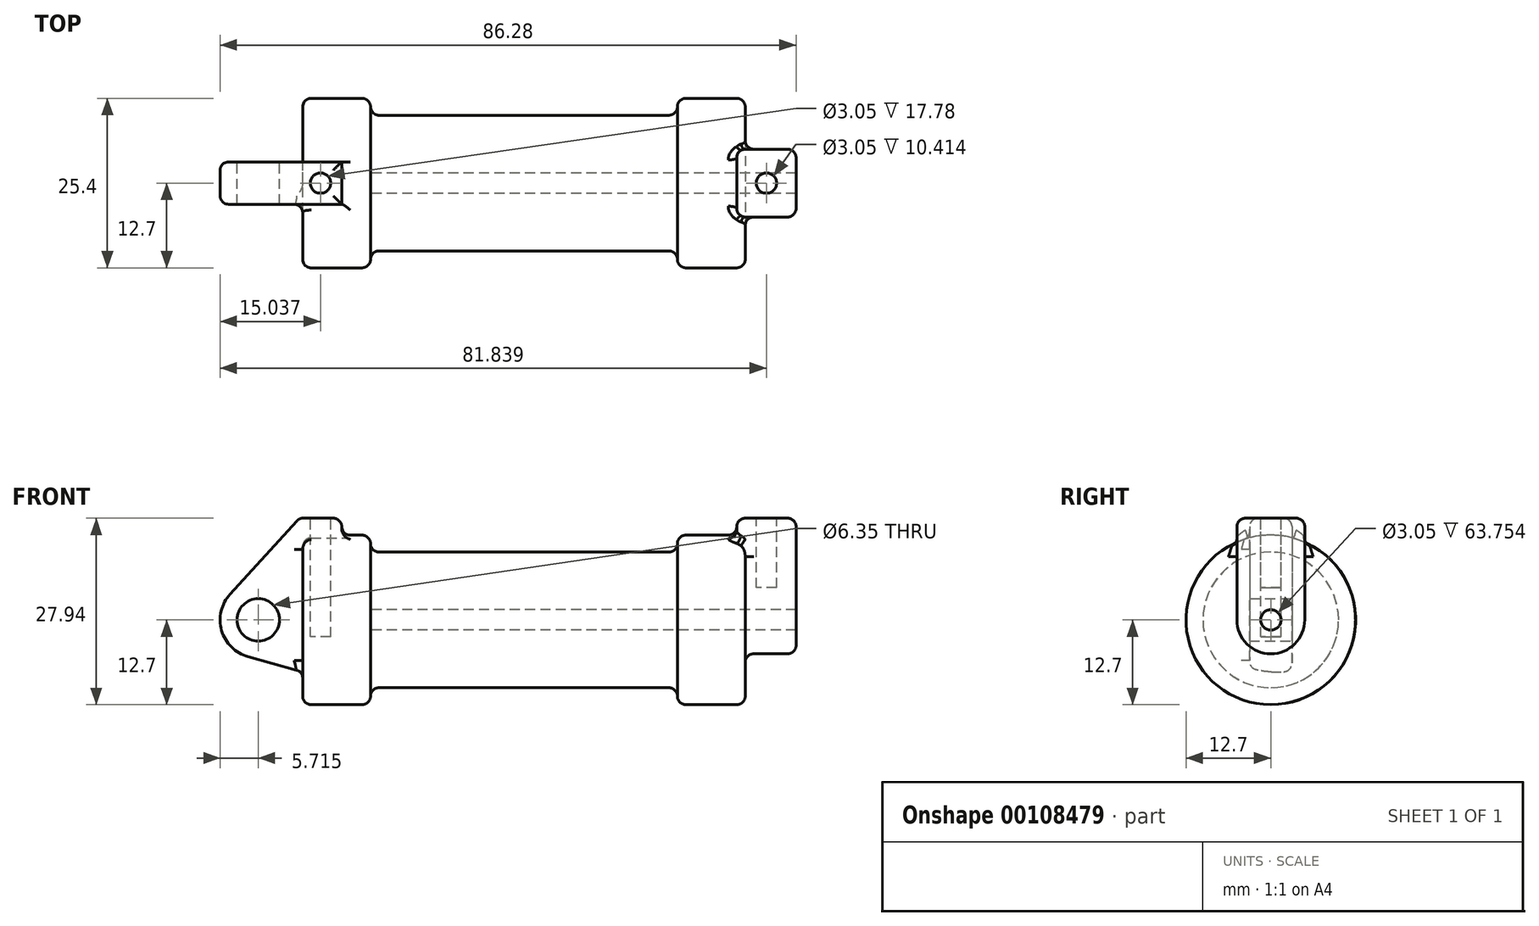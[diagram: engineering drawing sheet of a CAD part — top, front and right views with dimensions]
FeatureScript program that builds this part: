
annotation { "Feature Type Name" : "Feature", "Feature Type Description" : "" }
export const myFeature = defineFeature(function(context is Context, id is Id, definition is map)
    precondition{}
    {
        {
            var Q0;
            Q0=qCreatedBy(makeId("Front.planeOp"),FACE);
            var sketch = newSketch(context, id + "F0", { "sketchPlane" : qUnion([Q0])});
            skLineSegment(sketch, "E0", {"start": v(0, 0) * mm, "end": v(0, 12.7) * mm});
            skLineSegment(sketch, "E1", {"start": v(0, 12.7) * mm, "end": v(10.16, 12.7) * mm});
            skLineSegment(sketch, "E2", {"start": v(10.16, 12.7) * mm, "end": v(10.16, 10.16) * mm});
            skLineSegment(sketch, "E3", {"start": v(10.16, 10.16) * mm, "end": v(56.13, 10.16) * mm});
            skLineSegment(sketch, "E4", {"start": v(56.13, 10.16) * mm, "end": v(56.13, 12.7) * mm});
            skLineSegment(sketch, "E5", {"start": v(56.13, 12.7) * mm, "end": v(66.3, 12.7) * mm});
            skLineSegment(sketch, "E6", {"start": v(66.3, 12.7) * mm, "end": v(66.3, 0) * mm});
            skLineSegment(sketch, "E7", {"start": v(66.3, 0) * mm, "end": v(0, 0) * mm});
            skLineSegment(sketch, "E8", {"start": v(5.84, 15.24) * mm, "end": v(-0.5, 15.24) * mm});
            skLineSegment(sketch, "E9", {"start": v(-0.5, 15.24) * mm, "end": v(-10.88, 3.85) * mm});
            skLineSegment(sketch, "E10", {"start": v(0, 0) * mm, "end": v(-6.65, 0) * mm});
            skCircle(sketch, "E11", {"center": v(-6.65, 0) * mm, "radius": 5.72 * mm});
            skCircle(sketch, "E12", {"center": v(-6.65, 0) * mm, "radius": 3.18 * mm});
            skLineSegment(sketch, "E13", {"start": v(5.84, 15.24) * mm, "end": v(5.84, -9.4) * mm});
            skLineSegment(sketch, "E14", {"start": v(5.84, -9.4) * mm, "end": v(-8.18, -5.5) * mm});
            skSolve(sketch);
        }
        {
            var Q0;
            {var subQ0=sQuery(id+"F0.wireOp",EDGE,"E2");Q0=makeQuery(id+"F0.imprint","IMPRINT",FACE,{"disambiguationData":[TD([[makeQuery(id+"F0.imprint","IMPRINT",EDGE,{"derivedFrom":subQ0}),-1.0]])]});}
            var Q1;
            {var subQ0=sQuery(id+"F0.wireOp",EDGE,"E0");Q1=makeQuery(id+"F0.imprint","IMPRINT",FACE,{"disambiguationData":[TD([[makeQuery(id+"F0.imprint","IMPRINT",EDGE,{"derivedFrom":subQ0}),-1.0]])]});}
            var Q2;
            Q2=sQuery(id+"F0.wireOp",EDGE,"E7");
            revolve(context, id + "F1", {"entities" : qUnion([Q0, Q1]), "axis" : qUnion([Q2]), "revolveType" : RevolveType.FULL});
        }
        {
            var Q0;
            {var subQ3=sQuery(id+"F0.wireOp",EDGE,"E0");Q0=makeQuery(id+"F0.imprint","IMPRINT",FACE,{"disambiguationData":[TD([[makeQuery(id+"F0.imprint","IMPRINT",EDGE,{"derivedFrom":subQ3}),1.0]])]});}
            var Q1;
            {var subQ0=sQuery(id+"F0.wireOp",EDGE,"E14");Q1=makeQuery(id+"F0.imprint","IMPRINT",FACE,{"disambiguationData":[TD([[makeQuery(id+"F0.imprint","IMPRINT",EDGE,{"derivedFrom":subQ0}),-1.0]])]});}
            var Q2;
            {var subQ0=sQuery(id+"F0.wireOp",EDGE,"E0");Q2=makeQuery(id+"F0.imprint","IMPRINT",FACE,{"disambiguationData":[TD([[makeQuery(id+"F0.imprint","IMPRINT",EDGE,{"derivedFrom":subQ0}),-1.0]])]});}
            var Q3;
            {var subQ4=sQuery(id+"F0.wireOp",EDGE,"E12");Q3=makeQuery(id+"F0.imprint","IMPRINT",FACE,{"disambiguationData":[TD([[makeQuery(id+"F0.imprint","IMPRINT",EDGE,{"derivedFrom":subQ4}),-1.0]])]});}
            extrude(context, id + "F2", {"entities" : qUnion([Q0, Q1, Q2, Q3]), "operationType" : NewBodyOperationType.ADD, "endBound" : BoundingType.SYMMETRIC, "depth" : 6.35 * mm});
        }
        {
            var Q0;
            Q0=makeQuery(id+"F1.opRevolve","SWEPT_FACE",FACE,{"disambiguationData":[OSD([sQuery(id+"F0.wireOp",EDGE,"E6")])]});
            var sketch = newSketch(context, id + "F3", { "sketchPlane" : qUnion([Q0])});
            skCircle(sketch, "E15", {"center": v(0, 0) * mm, "radius": 5.08 * mm});
            skLineSegment(sketch, "E16", {"start": v(-5.08, 0) * mm, "end": v(-5.08, 15.24) * mm});
            skLineSegment(sketch, "E17", {"start": v(-5.08, 15.24) * mm, "end": v(5.08, 15.24) * mm});
            skLineSegment(sketch, "E18", {"start": v(5.08, 15.24) * mm, "end": v(5.08, 0) * mm});
            skCircle(sketch, "E19", {"center": v(0, 0) * mm, "radius": 1.52 * mm});
            skSolve(sketch);
        }
        {
            var Q0;
            {var subQ0=sQuery(id+"F3.wireOp",EDGE,"E17");Q0=makeQuery(id+"F3.imprint","IMPRINT",FACE,{"disambiguationData":[TD([[makeQuery(id+"F3.imprint","IMPRINT",EDGE,{"derivedFrom":subQ0}),-1.0]])]});}
            extrude(context, id + "F4", {"entities" : qUnion([Q0]), "operationType" : NewBodyOperationType.ADD, "oppositeDirection" : true, "depth" : 1.27 * mm});
        }
        {
            var Q0;
            Q0=makeQuery(id+"F4.opExtrude","CAP_FACE",FACE,{"disambiguationData":[OSD([sQuery(id+"F0.wireOp",EDGE,"E5"),sQuery(id+"F0.wireOp",EDGE,"E6"),sQuery(id+"F3.wireOp",EDGE,"E16"),sQuery(id+"F3.wireOp",EDGE,"E17"),sQuery(id+"F3.wireOp",EDGE,"E18")])],"isStart":false});
            var Q1;
            Q1 = qSketchRegion(id + "F3", true);
            extrude(context, id + "F5", {"entities" : qUnion([Q0, Q1]), "operationType" : NewBodyOperationType.ADD, "oppositeDirection" : true, "depth" : 7.62 * mm});
        }
        {
            var Q0;
            {var subQ0=sQuery(id+"F0.wireOp",EDGE,"E6");Q0=makeQuery(id+"F5.boolean.opBoolean","SPLIT",FACE,{"disambiguationData":[TD([makeQuery(id+"F5.opExtrude","SWEPT_FACE",FACE,{"disambiguationData":[OSD([sQuery(id+"F3.wireOp",EDGE,"E19")])]})])],"derivedFrom":makeQuery(id+"F4.boolean.opBoolean","MERGE",FACE,{"derivedFrom":[makeQuery(id+"F1.opRevolve","SWEPT_FACE",FACE,{"disambiguationData":[OSD([subQ0])]}),makeQuery(id+"F4.opExtrude","CAP_FACE",FACE,{"disambiguationData":[OSD([sQuery(id+"F0.wireOp",EDGE,"E5"),subQ0,sQuery(id+"F3.wireOp",EDGE,"E16"),sQuery(id+"F3.wireOp",EDGE,"E17"),sQuery(id+"F3.wireOp",EDGE,"E18")])],"isStart":true})]})});}
            var Q1;
            Q1=makeQuery(id+"F1.opRevolve","SWEPT_FACE",FACE,{"disambiguationData":[OSD([sQuery(id+"F0.wireOp",EDGE,"E2")])]});
            extrude(context, id + "F6", {"entities" : qUnion([Q0]), "operationType" : NewBodyOperationType.REMOVE, "endBound" : BoundingType.UP_TO_SURFACE, "oppositeDirection" : true, "endBoundEntityFace" : qUnion([Q1]), "depth" : 25.4 * mm});
        }
        {
            var Q0;
            Q0=makeQuery(id+"F2.opExtrude","SWEPT_FACE",FACE,{"disambiguationData":[OSD([sQuery(id+"F0.wireOp",EDGE,"E8")])]});
            var sketch = newSketch(context, id + "F7", { "sketchPlane" : qUnion([Q0])});
            skCircle(sketch, "E20", {"center": v(2.67, 0) * mm, "radius": 1.52 * mm});
            skPoint(sketch, "E20.centerSnap0", {"position": v(2.67, 3.18) * mm});
            skPoint(sketch, "E21.centerSnap0", {"position": v(5.84, 0) * mm});
            skSolve(sketch);
        }
        {
            var Q0;
            Q0 = qSketchRegion(id + "F7", true);
            extrude(context, id + "F8", {"entities" : qUnion([Q0]), "operationType" : NewBodyOperationType.REMOVE, "oppositeDirection" : true, "depth" : 17.78 * mm});
        }
        {
            var Q0;
            {var subQ0=sQuery(id+"F3.wireOp",EDGE,"E17");Q0=makeQuery(id+"FdJpuOExB23OV29_2.boolean.opBoolean","MERGE",FACE,{"derivedFrom":[makeQuery(id+"F4.opExtrude","SWEPT_FACE",FACE,{"disambiguationData":[OSD([subQ0])]}),makeQuery(id+"FdJpuOExB23OV29_2.opExtrude","SWEPT_FACE",FACE,{"disambiguationData":[OSD([subQ0]),TDD([makeQuery(id+"F3.imprint","IMPRINT",EDGE,{"derivedFrom":subQ0})])]}),makeQuery(id+"FdJpuOExB23OV29_2.opExtrude","SWEPT_FACE",FACE,{"disambiguationData":[OSD([subQ0]),TDD([makeQuery(id+"F4.opExtrude","CAP_EDGE",EDGE,{"disambiguationData":[OSD([subQ0])],"isStart":false})])]})]});}
            var sketch = newSketch(context, id + "F9", { "sketchPlane" : qUnion([Q0])});
            skCircle(sketch, "E22", {"center": v(69.47, 0) * mm, "radius": 1.52 * mm});
            skPoint(sketch, "E22.centerSnap0", {"position": v(69.47, 5.08) * mm});
            skSolve(sketch);
        }
        {
            var Q0;
            Q0 = qSketchRegion(id + "F9", true);
            extrude(context, id + "F10", {"entities" : qUnion([Q0]), "operationType" : NewBodyOperationType.REMOVE, "oppositeDirection" : true, "depth" : 10.4 * mm});
        }
        {
            var Q0;
            Q0=makeQuery(id+"F1.opRevolve","SWEPT_FACE",FACE,{"disambiguationData":[OSD([sQuery(id+"F0.wireOp",EDGE,"E3")])]});
            var Q1;
            Q1=makeQuery(id+"F1.opRevolve","SWEPT_EDGE",EDGE,{"disambiguationData":[OSD([sQuery(id+"F0.wireOp",EDGE,"E1"),sQuery(id+"F0.wireOp",EDGE,"E2")])]});
            var Q2;
            Q2=makeQuery(id+"F1.opRevolve","SWEPT_EDGE",EDGE,{"disambiguationData":[OSD([sQuery(id+"F0.wireOp",EDGE,"E4"),sQuery(id+"F0.wireOp",EDGE,"E5")])]});
            var Q3;
            Q3=makeQuery(id+"F1.opRevolve","SWEPT_EDGE",EDGE,{"disambiguationData":[OSD([sQuery(id+"F0.wireOp",EDGE,"E0"),sQuery(id+"F0.wireOp",EDGE,"E1")])]});
            var Q4;
            Q4=makeQuery(id+"FdJpuOExB23OV29_2.boolean.opBoolean","SPLIT",EDGE,{"disambiguationData":[OD(1.0)],"derivedFrom":makeQuery(id+"F1.opRevolve","SWEPT_EDGE",EDGE,{"disambiguationData":[OSD([sQuery(id+"F0.wireOp",EDGE,"E5"),sQuery(id+"F0.wireOp",EDGE,"E6")])]})});
            fillet(context, id + "F11", {"entities" : qUnion([Q0, Q1, Q2, Q3, Q4]), "radius" : 1.27 * mm, "tangentPropagation" : true, "allowEdgeOverflow" : false});
        }
        {
            var Q0;
            Q0=makeQuery(id+"F2.opExtrude","SWEPT_FACE",FACE,{"disambiguationData":[OSD([sQuery(id+"F0.wireOp",EDGE,"E9")])]});
            var Q1;
            Q1=makeQuery(id+"F2.opExtrude","CAP_EDGE",EDGE,{"disambiguationData":[OSD([sQuery(id+"F0.wireOp",EDGE,"E8")])],"isStart":false});
            var Q2;
            Q2=makeQuery(id+"F2.opExtrude","SWEPT_EDGE",EDGE,{"disambiguationData":[OSD([sQuery(id+"F0.wireOp",EDGE,"E8"),sQuery(id+"F0.wireOp",EDGE,"E13")])]});
            var Q3;
            Q3=makeQuery(id+"F2.opExtrude","CAP_EDGE",EDGE,{"disambiguationData":[OSD([sQuery(id+"F0.wireOp",EDGE,"E8")])],"isStart":true});
            var Q4;
            Q4=makeQuery(id+"F2.boolean.opBoolean","INTERSECT",EDGE,{"derivedFrom":[makeQuery(id+"F1.opRevolve","SWEPT_FACE",FACE,{"disambiguationData":[OSD([sQuery(id+"F0.wireOp",EDGE,"E1")])]}),makeQuery(id+"F2.opExtrude","CAP_FACE",FACE,{"disambiguationData":[OSD([sQuery(id+"F0.wireOp",EDGE,"E8"),sQuery(id+"F0.wireOp",EDGE,"E9"),sQuery(id+"F0.wireOp",EDGE,"E11"),sQuery(id+"F0.wireOp",EDGE,"E12"),sQuery(id+"F0.wireOp",EDGE,"E13"),sQuery(id+"F0.wireOp",EDGE,"E14")])],"isStart":false})]});
            var Q5;
            Q5=makeQuery(id+"F2.boolean.opBoolean","INTERSECT",EDGE,{"derivedFrom":[makeQuery(id+"F1.opRevolve","SWEPT_FACE",FACE,{"disambiguationData":[OSD([sQuery(id+"F0.wireOp",EDGE,"E1")])]}),makeQuery(id+"F2.opExtrude","SWEPT_FACE",FACE,{"disambiguationData":[OSD([sQuery(id+"F0.wireOp",EDGE,"E13")])]})]});
            fillet(context, id + "F12", {"entities" : qUnion([Q0, Q1, Q2, Q3, Q4, Q5]), "radius" : 1.27 * mm, "tangentPropagation" : true, "allowEdgeOverflow" : false});
        }
        {
            var Q0;
            Q0=makeQuery(id+"F4.opExtrude","CAP_FACE",FACE,{"disambiguationData":[OSD([sQuery(id+"F0.wireOp",EDGE,"E5"),sQuery(id+"F0.wireOp",EDGE,"E6"),sQuery(id+"F3.wireOp",EDGE,"E16"),sQuery(id+"F3.wireOp",EDGE,"E17"),sQuery(id+"F3.wireOp",EDGE,"E18")])],"isStart":false});
            var Q1;
            {var subQ0=sQuery(id+"F3.wireOp",EDGE,"E18");var subQ1=sQuery(id+"F3.wireOp",EDGE,"E17");Q1=makeQuery(id+"F5.boolean.opBoolean","MERGE",EDGE,{"derivedFrom":[makeQuery(id+"F4.opExtrude","SWEPT_EDGE",EDGE,{"disambiguationData":[OSD([subQ1,subQ0])]}),makeQuery(id+"F5.opExtrude","SWEPT_EDGE",EDGE,{"disambiguationData":[OSD([subQ1,subQ0]),TDD([makeQuery(id+"F3.imprint","INTERSECT",VERTEX,{"derivedFrom":[subQ1,subQ0]})])]}),makeQuery(id+"F5.opExtrude","SWEPT_EDGE",EDGE,{"disambiguationData":[OSD([subQ1,subQ0]),TDD([makeQuery(id+"F4.opExtrude","CAP_VERTEX",VERTEX,{"disambiguationData":[OSD([subQ1,subQ0])],"isStart":false})])]})]});}
            var Q2;
            {var subQ0=sQuery(id+"F3.wireOp",EDGE,"E17");var subQ1=sQuery(id+"F3.wireOp",EDGE,"E16");Q2=makeQuery(id+"F5.boolean.opBoolean","MERGE",EDGE,{"derivedFrom":[makeQuery(id+"F4.opExtrude","SWEPT_EDGE",EDGE,{"disambiguationData":[OSD([subQ1,subQ0])]}),makeQuery(id+"F5.opExtrude","SWEPT_EDGE",EDGE,{"disambiguationData":[OSD([subQ1,subQ0]),TDD([makeQuery(id+"F3.imprint","INTERSECT",VERTEX,{"derivedFrom":[subQ1,subQ0]})])]}),makeQuery(id+"F5.opExtrude","SWEPT_EDGE",EDGE,{"disambiguationData":[OSD([subQ1,subQ0]),TDD([makeQuery(id+"F4.opExtrude","CAP_VERTEX",VERTEX,{"disambiguationData":[OSD([subQ1,subQ0])],"isStart":false})])]})]});}
            var Q3;
            {var subQ0=sQuery(id+"F3.wireOp",EDGE,"E18");Q3=makeQuery(id+"F5.boolean.opBoolean","MERGE",FACE,{"derivedFrom":[makeQuery(id+"F4.opExtrude","SWEPT_FACE",FACE,{"disambiguationData":[OSD([subQ0])]}),makeQuery(id+"F5.opExtrude","SWEPT_FACE",FACE,{"disambiguationData":[OSD([subQ0]),TDD([makeQuery(id+"F3.imprint","IMPRINT",EDGE,{"disambiguationData":[TD([[makeQuery(id+"F3.imprint","INTERSECT",VERTEX,{"derivedFrom":[sQuery(id+"F3.wireOp",EDGE,"E17"),subQ0]}),-1.0]])],"derivedFrom":subQ0}),makeQuery(id+"F3.imprint","IMPRINT",EDGE,{"disambiguationData":[TD([[makeQuery(id+"F3.imprint","INTERSECT",VERTEX,{"derivedFrom":[sQuery(id+"F3.wireOp",EDGE,"E15"),subQ0]}),1.0]])],"derivedFrom":subQ0})])]}),makeQuery(id+"F5.opExtrude","SWEPT_FACE",FACE,{"disambiguationData":[OSD([subQ0]),TDD([makeQuery(id+"F4.opExtrude","CAP_EDGE",EDGE,{"disambiguationData":[OSD([subQ0])],"isStart":false})])]})]});}
            var Q4;
            {var subQ0=sQuery(id+"F3.wireOp",EDGE,"E17");Q4=makeQuery(id+"F5.opExtrude","CAP_EDGE",EDGE,{"disambiguationData":[OSD([subQ0]),TDD([makeQuery(id+"F3.imprint","IMPRINT",EDGE,{"derivedFrom":subQ0})])],"isStart":false});}
            fillet(context, id + "F13", {"entities" : qUnion([Q0, Q1, Q2, Q3, Q4]), "radius" : 1.27 * mm, "tangentPropagation" : true, "allowEdgeOverflow" : false});
        }
    });
